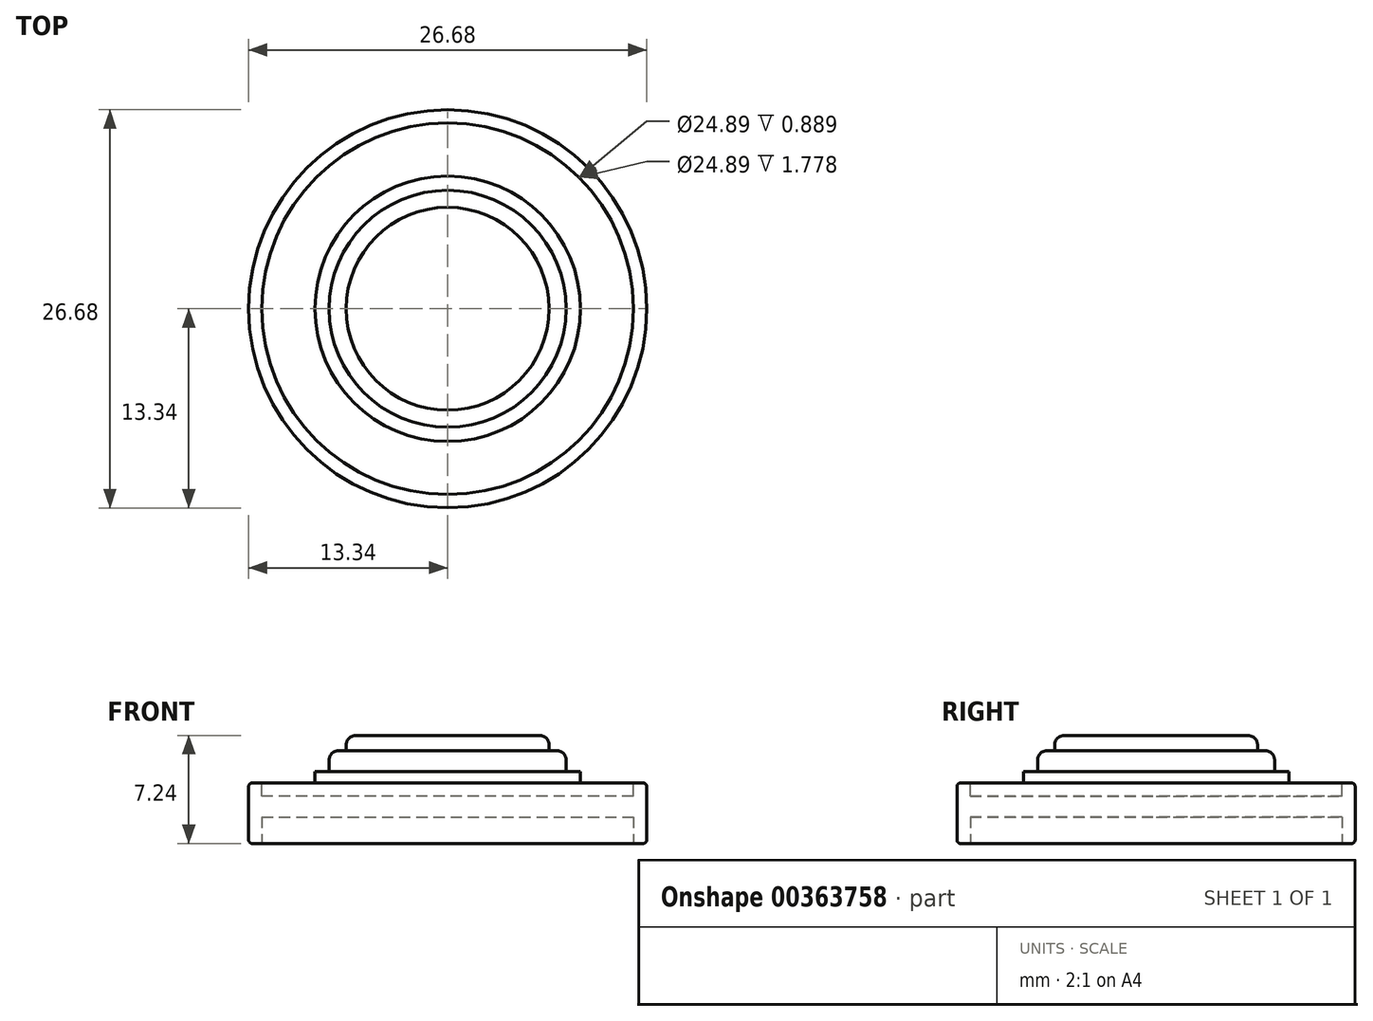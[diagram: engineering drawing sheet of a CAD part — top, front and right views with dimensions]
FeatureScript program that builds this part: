
annotation { "Feature Type Name" : "Feature", "Feature Type Description" : "" }
export const myFeature = defineFeature(function(context is Context, id is Id, definition is map)
    precondition{}
    {
        {
            var Q0;
            Q0=qCreatedBy(makeId("Top.planeOp"),FACE);
            var sketch = newSketch(context, id + "F0", { "sketchPlane" : qUnion([Q0])});
            skCircle(sketch, "E0", {"center": v(0, 0) * mm, "radius": 13.34 * mm});
            skSolve(sketch);
        }
        {
            var Q0;
            Q0 = qSketchRegion(id + "F0", true);
            extrude(context, id + "F1", {"entities" : qUnion([Q0]), "depth" : 4.06 * mm});
        }
        {
            var Q0;
            Q0=makeQuery(id+"F1.opExtrude","CAP_FACE",FACE,{"disambiguationData":[OSD([sQuery(id+"F0.wireOp",EDGE,"E0")])],"isStart":false});
            var sketch = newSketch(context, id + "F2", { "sketchPlane" : qUnion([Q0])});
            skCircle(sketch, "E1", {"center": v(0, 0) * mm, "radius": 8.9 * mm});
            skSolve(sketch);
        }
        {
            var Q0;
            Q0 = qSketchRegion(id + "F2", true);
            extrude(context, id + "F3", {"entities" : qUnion([Q0]), "operationType" : NewBodyOperationType.ADD, "depth" : 0.76 * mm});
        }
        {
            var Q0;
            Q0=makeQuery(id+"F1.opExtrude","CAP_FACE",FACE,{"disambiguationData":[OSD([sQuery(id+"F0.wireOp",EDGE,"E0")])],"isStart":false});
            var sketch = newSketch(context, id + "F4", { "sketchPlane" : qUnion([Q0])});
            skCircle(sketch, "E2", {"center": v(0, 0) * mm, "radius": 7.94 * mm});
            skSolve(sketch);
        }
        {
            var Q0;
            Q0 = qSketchRegion(id + "F4", true);
            extrude(context, id + "F5", {"entities" : qUnion([Q0]), "operationType" : NewBodyOperationType.ADD, "depth" : 2.16 * mm});
        }
        {
            var Q0;
            Q0=makeQuery(id+"F1.opExtrude","CAP_FACE",FACE,{"disambiguationData":[OSD([sQuery(id+"F0.wireOp",EDGE,"E0")])],"isStart":false});
            var sketch = newSketch(context, id + "F6", { "sketchPlane" : qUnion([Q0])});
            skCircle(sketch, "E3", {"center": v(0, 0) * mm, "radius": 6.8 * mm});
            skSolve(sketch);
        }
        {
            var Q0;
            Q0 = qSketchRegion(id + "F6", true);
            extrude(context, id + "F7", {"entities" : qUnion([Q0]), "operationType" : NewBodyOperationType.ADD, "depth" : 3.17 * mm});
        }
        {
            var Q0;
            Q0=makeQuery(id+"F5.opExtrude","CAP_EDGE",EDGE,{"disambiguationData":[OSD([sQuery(id+"F4.wireOp",EDGE,"E2")])],"isStart":false});
            var Q1;
            Q1=makeQuery(id+"F7.opExtrude","CAP_EDGE",EDGE,{"disambiguationData":[OSD([sQuery(id+"F6.wireOp",EDGE,"E3")])],"isStart":false});
            fillet(context, id + "F8", {"entities" : qUnion([Q0, Q1]), "radius" : 0.64 * mm, "tangentPropagation" : true, "allowEdgeOverflow" : false});
        }
        {
            var Q0;
            Q0=makeQuery(id+"F1.opExtrude","CAP_FACE",FACE,{"disambiguationData":[OSD([sQuery(id+"F0.wireOp",EDGE,"E0")])],"isStart":false});
            var sketch = newSketch(context, id + "F9", { "sketchPlane" : qUnion([Q0])});
            skCircle(sketch, "E4", {"center": v(0, 0) * mm, "radius": 12.45 * mm});
            skSolve(sketch);
        }
        {
            var Q0;
            Q0 = qSketchRegion(id + "F9", true);
            extrude(context, id + "F10", {"entities" : qUnion([Q0]), "operationType" : NewBodyOperationType.REMOVE, "oppositeDirection" : true, "depth" : 0.89 * mm});
        }
        {
            var Q0;
            Q0=makeQuery(id+"F1.opExtrude","CAP_FACE",FACE,{"disambiguationData":[OSD([sQuery(id+"F0.wireOp",EDGE,"E0")])],"isStart":true});
            var sketch = newSketch(context, id + "F11", { "sketchPlane" : qUnion([Q0])});
            skCircle(sketch, "E5", {"center": v(0, 0) * mm, "radius": 12.45 * mm});
            skSolve(sketch);
        }
        {
            var Q0;
            Q0 = qSketchRegion(id + "F11", true);
            extrude(context, id + "F12", {"entities" : qUnion([Q0]), "operationType" : NewBodyOperationType.REMOVE, "oppositeDirection" : true, "depth" : 1.78 * mm});
        }
        {
            var Q0;
            Q0=makeQuery(id+"F10.boolean.opBoolean","COPY",EDGE,{"derivedFrom":makeQuery(id+"F10.opExtrude","CAP_EDGE",EDGE,{"disambiguationData":[OSD([sQuery(id+"F9.wireOp",EDGE,"E4")])],"isStart":true})});
            var Q1;
            Q1=makeQuery(id+"F1.opExtrude","CAP_EDGE",EDGE,{"disambiguationData":[OSD([sQuery(id+"F0.wireOp",EDGE,"E0")])],"isStart":false});
            var Q2;
            Q2=makeQuery(id+"F1.opExtrude","CAP_EDGE",EDGE,{"disambiguationData":[OSD([sQuery(id+"F0.wireOp",EDGE,"E0")])],"isStart":true});
            var Q3;
            Q3=makeQuery(id+"F12.boolean.opBoolean","COPY",EDGE,{"derivedFrom":makeQuery(id+"F12.opExtrude","CAP_EDGE",EDGE,{"disambiguationData":[OSD([sQuery(id+"F11.wireOp",EDGE,"E5")])],"isStart":true})});
            fillet(context, id + "F13", {"entities" : qUnion([Q0, Q1, Q2, Q3]), "radius" : 0.25 * mm, "tangentPropagation" : true, "allowEdgeOverflow" : false});
        }
    });
